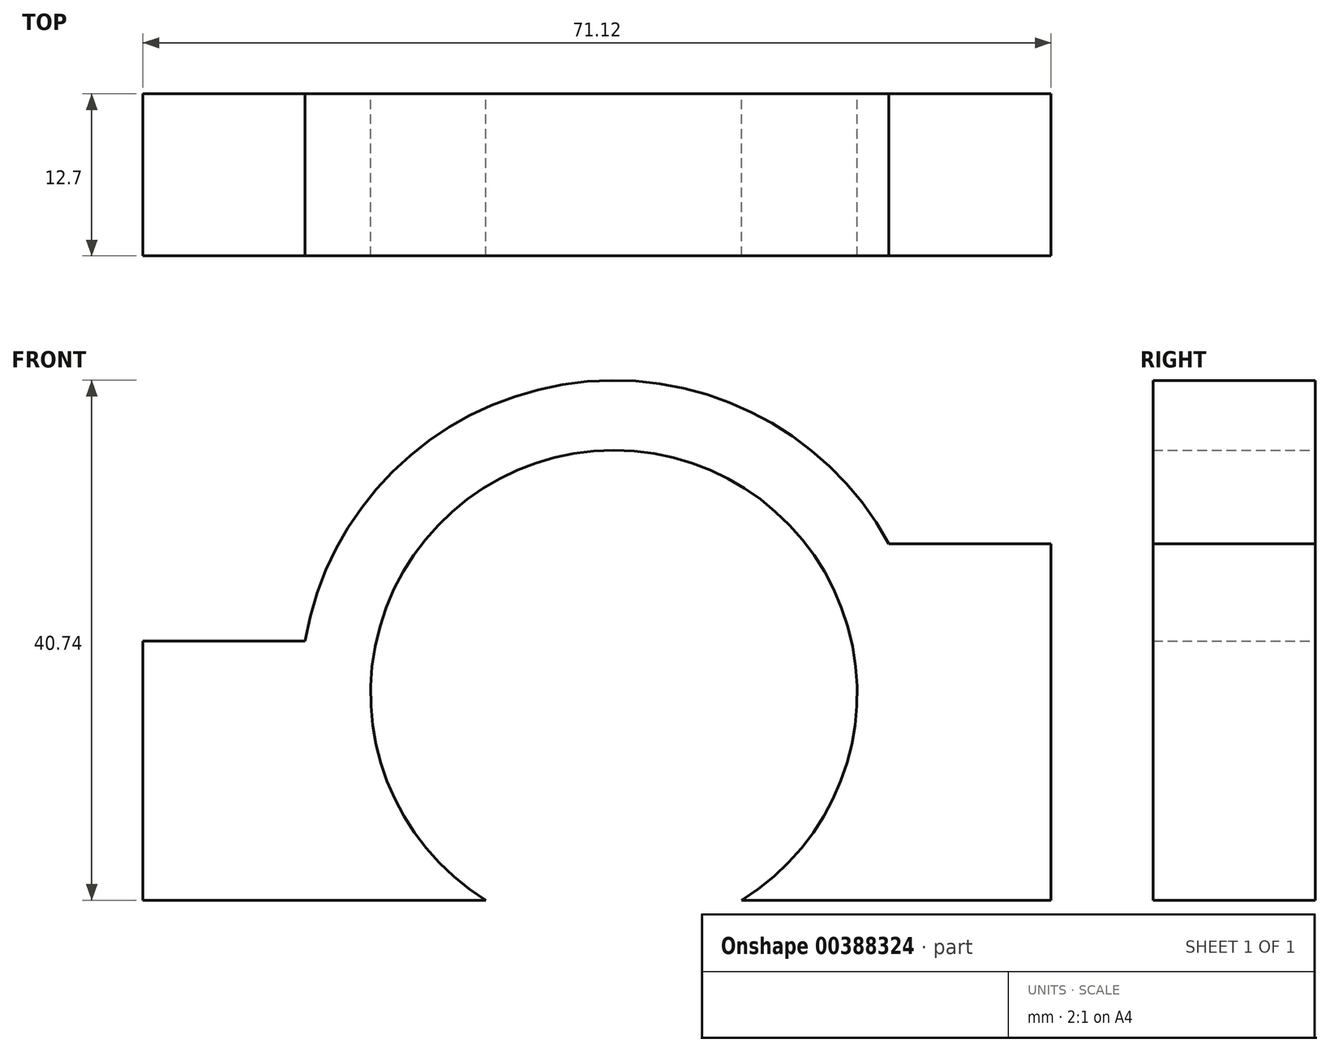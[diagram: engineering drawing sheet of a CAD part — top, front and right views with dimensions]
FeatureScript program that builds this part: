
annotation { "Feature Type Name" : "Feature", "Feature Type Description" : "" }
export const myFeature = defineFeature(function(context is Context, id is Id, definition is map)
    precondition{}
    {
        {
            var Q0;
            Q0=qCreatedBy(makeId("Front.planeOp"),FACE);
            var sketch = newSketch(context, id + "F0", { "sketchPlane" : qUnion([Q0])});
            skLineSegment(sketch, "E0", {"start": v(-15.84, 15.85) * mm, "end": v(-15.84, -4.47) * mm});
            skLineSegment(sketch, "E1", {"start": v(-15.84, -4.47) * mm, "end": v(55.28, -4.47) * mm});
            skLineSegment(sketch, "E2", {"start": v(55.28, -4.47) * mm, "end": v(55.28, 23.47) * mm});
            skLineSegment(sketch, "E3", {"start": v(55.28, 23.47) * mm, "end": v(42.58, 23.47) * mm});
            skLineSegment(sketch, "E4", {"start": v(-15.84, 15.85) * mm, "end": v(-3.14, 15.85) * mm});
            skArc(sketch, "E5", {"start": v(42.58, 23.47) * mm, "mid": v(17, 35.93) * mm, "end": v(-3.14, 15.85) * mm});
            skCircle(sketch, "E6", {"center": v(21.04, 11.74) * mm, "radius": 19.05 * mm});
            skSolve(sketch);
        }
        {
            var Q0;
            {var subQ0=sQuery(id+"F0.wireOp",EDGE,"E6");var subQ1=sQuery(id+"F0.wireOp",EDGE,"E1");var subQ2=makeQuery(id+"F0.imprint","INTERSECT",VERTEX,{"disambiguationData":[OD(0.0)],"derivedFrom":[subQ1,subQ0]});Q0=makeQuery(id+"F0.imprint","IMPRINT",FACE,{"disambiguationData":[TD([[makeQuery(id+"F0.imprint","IMPRINT",EDGE,{"disambiguationData":[TD([[subQ2,-1.0]])],"derivedFrom":subQ1}),-1.0]])]});}
            var Q1;
            {var subQ4=sQuery(id+"F0.wireOp",EDGE,"E0");Q1=makeQuery(id+"F0.imprint","IMPRINT",FACE,{"disambiguationData":[TD([[makeQuery(id+"F0.imprint","IMPRINT",EDGE,{"derivedFrom":subQ4}),1.0]])]});}
            extrude(context, id + "F1", {"entities" : qUnion([Q0, Q1]), "depth" : 12.7 * mm});
        }
        {
            var Q0;
            Q0=makeQuery(id+"F1.opExtrude","SWEPT_BODY",BODY,{"disambiguationData":[OSD([sQuery(id+"F0.wireOp",EDGE,"E1"),sQuery(id+"F0.wireOp",EDGE,"E6")])]});
            deleteBodies(context, id + "F2", {"entities" : qUnion([Q0])});
        }
    });
